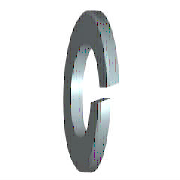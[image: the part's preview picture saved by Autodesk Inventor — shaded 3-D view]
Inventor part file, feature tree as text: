
AUTODESK INVENTOR PART (.ipt)
format: ipt  version: 2025 (Build 290162000, 162)  size: 126,976 bytes
history: native  units: mm (DEFAULTED — no unit token found)
features: extrude x2, other x1, plane x1
ambient origin geometry x6: Origin, YZ Plane, X Axis, Y Axis, Z Axis, Center Point
bodies: Solid1 (feature_tree)
feature tree (4):
  extrude  "轴承体"  Depth=10.2mm
  extrude  "切口"  Depth=15.4mm
  other  "Work Axis1"
  plane  "Work Plane1"
